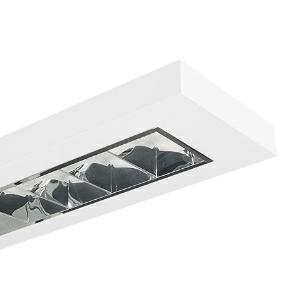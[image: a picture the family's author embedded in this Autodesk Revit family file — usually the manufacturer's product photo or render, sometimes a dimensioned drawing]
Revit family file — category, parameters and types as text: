
# Revit family: 3f_filippi_-_3f_travetta_di_2mg_3f_filippi_-_10747_-_3f_travetta_led_di_2x15w_2mg_l1590
name_source: partatom
category: Lighting Fixtures
units: mm (PartAtom-declared; Revit-internal decimal feet)

## family parameters
Cut with Voids When Loaded = No
Host = Face
Light Source = No
Part Type = Normal
Room Calculation Point = No
Round Connector Dimension = Use Diameter
Shared = No

## types (1)
- 3F Filippi - 3F Travetta DI 2MG (1 x LED, 3958 lm, 33 W, 4000 K)
    Apparent Load = 33 VA
    Approval mark = ENEC
    CIE Flux Codes = 61 98 100 85 100
    Color Rendering = 80
    Color Temperature = 4000 K
    Control Gear = Electronic ballast
    Default Elevation = 1800 mm
    Description = ILLUMINOTECHNICAL
Luminous efficiency 100% (DLOR 85%, ULOR 15%).
Initial luminous flux of the luminaire 3958 lm.
Symmetric direct-indirect distribution.
Installation Interdistance Transv.D = 2.02 x hu - Long.D = 1.27 x hu.
Average luminance <1000 cd/m² for radial angles >65°.
Tabular UGR (CIE 117 - 4H-8H; S=0.25H; 70/50/20): RUG 17.1 - 16.4.
Beam angle: 99° - 72°.
Luminous efficacy 120 lm/W.
Lifetime (L93/B10): 30000 h. (tq+25°C)
Lifetime (L90/B10): 50000 h. (tq+25°C)
Lifetime (L85/B10): 80000 h. (tq+25°C)
Lifetime (L80/B10): 100000 h. (tq+25°C)
Sudden decreased luminous flux after 50000 hours: 0% (C0).
Photobiological safety in compliance with IEC/TR 62778: RG0 risk exempt, (IEC 62471).
In compliance with IEC/EN 62722-2-1 - IEC/EN 62717 standards.

SOURCE
2 linear LED modules 15W/840.
Energy efficiency class (UE 2019/2020 - UE 2019/2015): D.
CIE 13.3 Colour rendering index: CRI >80 (R9 <50%).
IES TM-30 Fidelity Index: Rf = 84 Rg = 95.
CCT nominal colour temperature 4000 K.
Colour initial tolerance (MacAdam): SDCM 2.

MECHANICAL
Housing with squared shape in white painted galvannealed steel, with nonreflecting surface.
2MG parabolic louvre, high efficiency, in specular aluminium with superficial titanium-magnesium treatment, non-iridescent, with transverse blades closed at the top.
Prismatic flat diffuser in transparent methacrylate (PMMA), multilenticular, anti-glare, prismatic exterior, placed above louvre blades.
Film protective against dust and finger marks, adhesive, attached to louvre.
Upper holes closing film made of opal polycarbonate.
Luminaire with limited surface temperature. - D - (EN 60598-2-24)
Dimensions: 1590x190 mm, height 60 mm (edge 40 mm). Weight 5.03 kg.
IP20 protection degree.
Mechanical strength to impacts IK02 (0.2 joule).
Glow-wire test resistance 650°C.

ELECTRICAL
Halogen Free electronic wiring 230V-50/60Hz, power factor 0.95, THD <25%, constant output current, SELV, class I, 1 driver.
Power of the luminaire 33 W.
CE - IEC 60598-1 - EN 60598-1.
SAFE FLICKER: PstLM=<1 and SVM=<0.4 (IEC TR 61547-1 and IEC TR 63158), to ensure a more comfortable and safe light.
Luminaire compliant with EN 60598-2-22 for power supply from a centralised emergency system CPSS (Central Power Supply System), not incorporated in the luminaire - high risk areas excluded. The default power and flux are 100% in AC and 100% in DC.
Ambient temperature from 0°C to +25°C.
Temperature class T6 max 85°C.
Relative humidity UR: <85%.

INSTALLATION
Suspended.
All accessories dedicated to this product are available on the Catalog and on our website www.3F-Filippi.com.

APPLICATIONS
In environments, even with reduced height, requiring a comfortable light.
In environments with VDTs, managerial offices and staterooms, public offices and schools.

WARNING
Luminaire designed for disposal/recycling at end-of-life.
Replaceable (LED only) light source by a professional. Replaceable control gear by a professional.
    Height = 60 mm  [stored 0.19685 ft]
    Lamp = 1 x LED
    Lamp Light Flux = 3958 lm
    Lamp Power = 33 W
    Lamp count = 1
    Length = 1590 mm
    Lifetime = 50000 h
    Luminous efficacy = 120 lm/W
    Manufacturer = 3F Filippi
    ModVariant = No
    Model = 3F Filippi - 10747 - 3F Travetta LED DI 2x15W 2MG L1590
    Mounting Place = Ceiling
    Mounting Type = Pendant
    Number of Poles = 1
    OnlyDefault = Yes
    Power Factor = 1
    Product Name = 3F Filippi - 3F Travetta DI 2MG
    Product group = pendant luminaire
    ProductGroupID = 9
    Protection Class = Protection class I
    Protection Degree = IP 20
    RLX_Detail_Level = 1
    RLX_Emergency_Light_Flux = 0 lm
    RLX_Emergency_Type = 0
    RLX_Emergency_Type_DB = No
    RlxData = <blob elided: 51265 chars, md5=7c4093f7>
    Socket = socket
    Standby Power = 0 W
    System Light Flux = 3958 lm
    System Power = 33 W
    Type Comments = Product without accessories
    Type Image = 3ffilippi_3f_travetta_led_2mg.jpg
    URL = http://relux.com
    VarID = ---
    Voltage = 0 V
    Weight = 0.00 kg
    Width = 190 mm  [stored 0.62336 ft]

note: [stored X ft] marks values corroborated as IEEE doubles in the binary element streams (Revit-internal decimal feet)

## geometry (parser evidence)
native form markers: Blend x4, Sweep x12
no freeform markers — native parametric forms only
